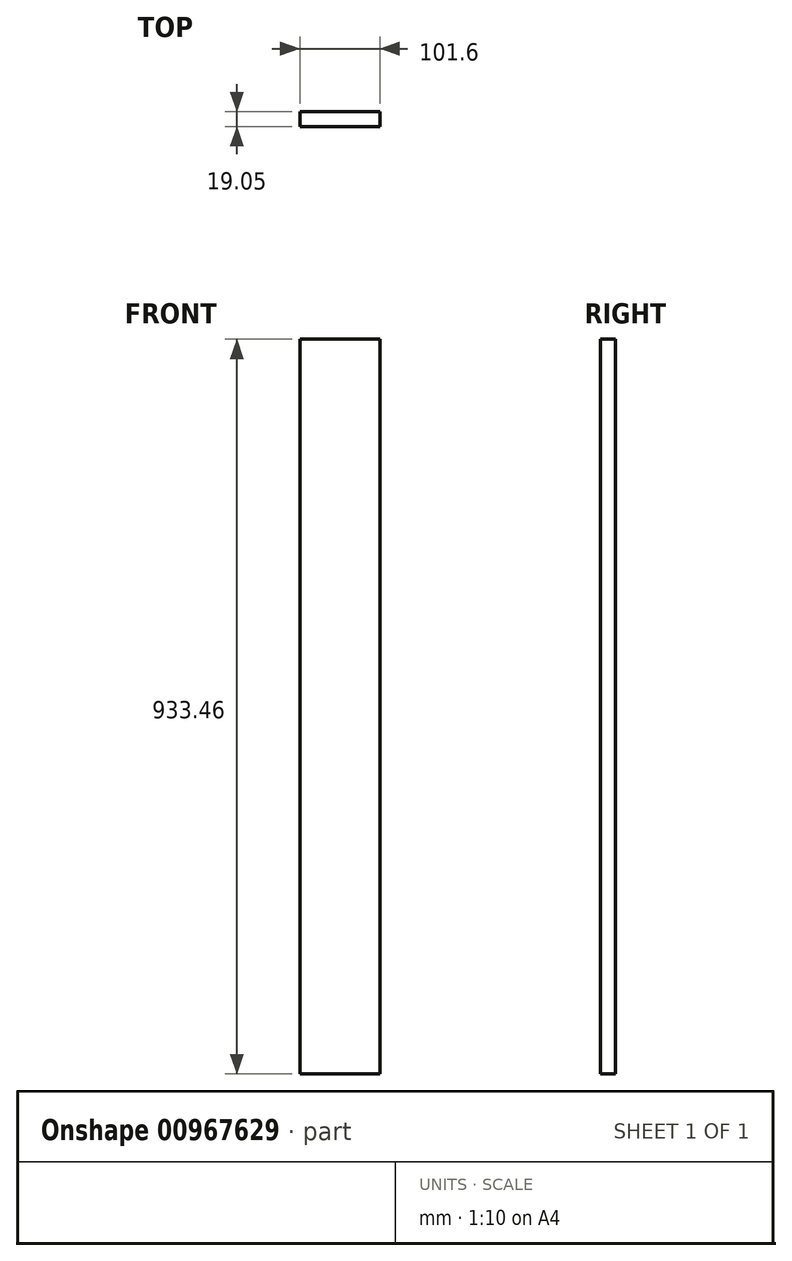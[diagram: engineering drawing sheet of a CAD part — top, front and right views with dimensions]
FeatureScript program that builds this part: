
annotation { "Feature Type Name" : "Feature", "Feature Type Description" : "" }
export const myFeature = defineFeature(function(context is Context, id is Id, definition is map)
    precondition{}
    {
        {
            var Q0;
            Q0=qCreatedBy(makeId("Front.planeOp"),FACE);
            var sketch = newSketch(context, id + "F0", { "sketchPlane" : qUnion([Q0])});
            skLineSegment(sketch, "E0.bottom", {"start": v(50.8, 466.72) * mm, "end": v(-50.8, 466.72) * mm});
            skLineSegment(sketch, "E0.top", {"start": v(50.8, -466.73) * mm, "end": v(-50.8, -466.73) * mm});
            skLineSegment(sketch, "E0.left", {"start": v(50.8, 466.72) * mm, "end": v(50.8, -466.73) * mm});
            skLineSegment(sketch, "E0.right", {"start": v(-50.8, 466.72) * mm, "end": v(-50.8, -466.73) * mm});
            skPoint(sketch, "E0.middle", {"position": v(0, 0) * mm});
            skSolve(sketch);
        }
        {
            var Q0;
            Q0 = qSketchRegion(id + "F0", true);
            extrude(context, id + "F1", {"entities" : qUnion([Q0]), "depth" : 19.05 * mm, "offsetDistance" : 25.4 * mm});
        }
    });
